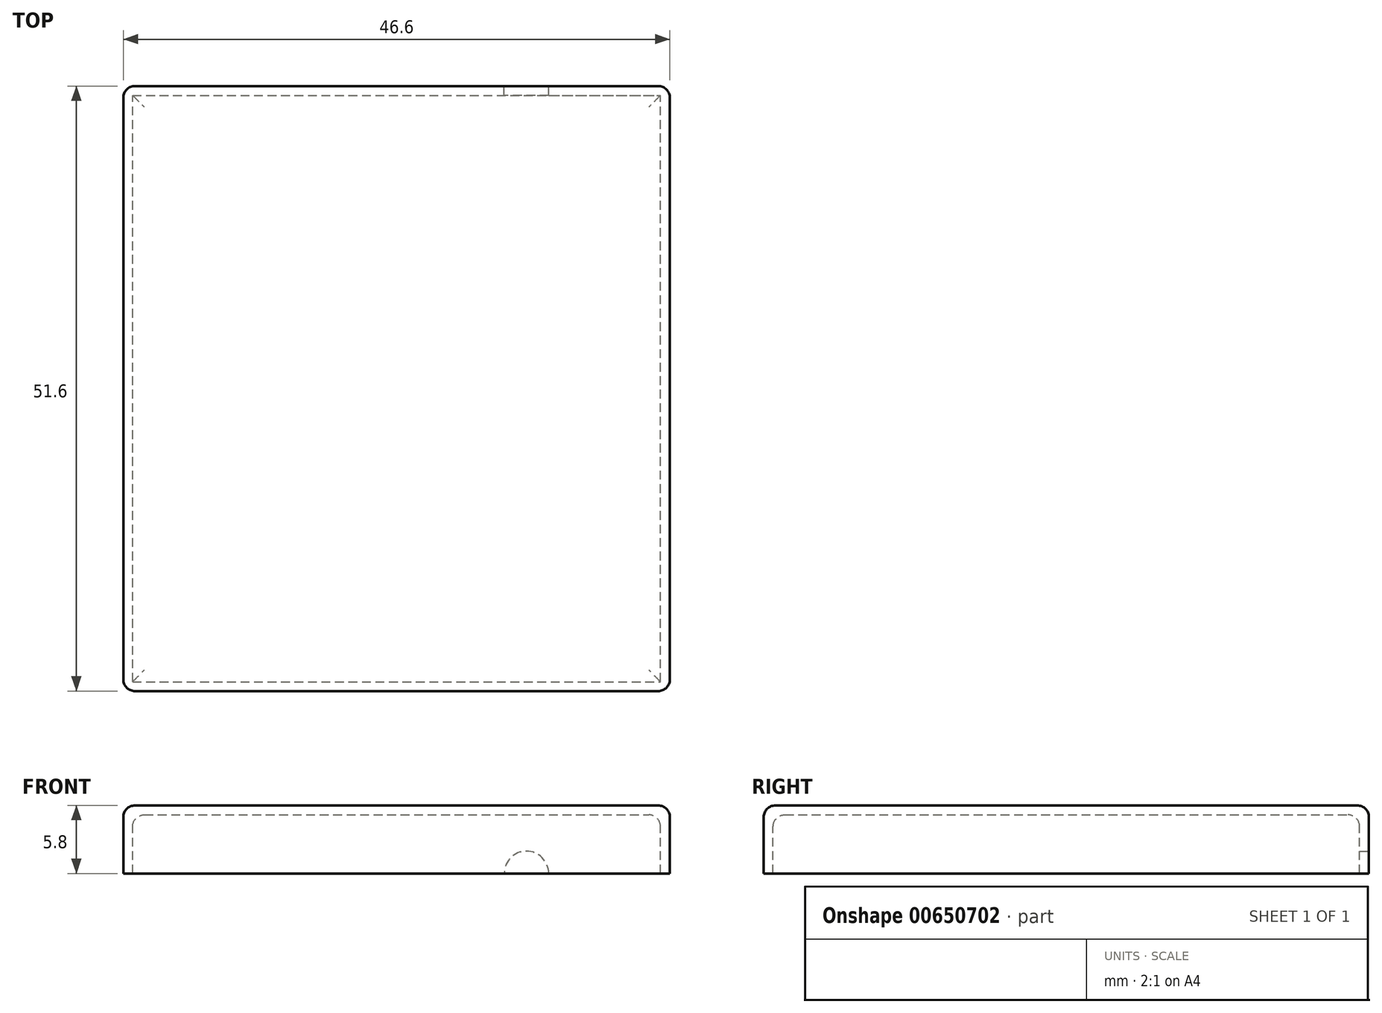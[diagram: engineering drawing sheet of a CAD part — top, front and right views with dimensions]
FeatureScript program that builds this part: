
annotation { "Feature Type Name" : "Feature", "Feature Type Description" : "" }
export const myFeature = defineFeature(function(context is Context, id is Id, definition is map)
    precondition{}
    {
        {
            var Q0;
            Q0=qCreatedBy(makeId("Top.planeOp"),FACE);
            var sketch = newSketch(context, id + "F0", { "sketchPlane" : qUnion([Q0])});
            skLineSegment(sketch, "E0.bottom", {"start": v(0, 0) * mm, "end": v(45, 0) * mm});
            skLineSegment(sketch, "E0.top", {"start": v(0, 50) * mm, "end": v(45, 50) * mm});
            skLineSegment(sketch, "E0.left", {"start": v(0, 0) * mm, "end": v(0, 50) * mm});
            skLineSegment(sketch, "E0.right", {"start": v(45, 0) * mm, "end": v(45, 50) * mm});
            skLineSegment(sketch, "E1.0", {"start": v(-0.8, -0.8) * mm, "end": v(-0.8, 50.8) * mm});
            skLineSegment(sketch, "E1.1", {"start": v(-0.8, -0.8) * mm, "end": v(45.8, -0.8) * mm});
            skLineSegment(sketch, "E1.2", {"start": v(45.8, -0.8) * mm, "end": v(45.8, 50.8) * mm});
            skLineSegment(sketch, "E1.3", {"start": v(-0.8, 50.8) * mm, "end": v(45.8, 50.8) * mm});
            skSolve(sketch);
        }
        {
            var Q0;
            Q0=makeQuery(id+"F0.imprint","IMPRINT",FACE,{"disambiguationData":[TD([[makeQuery(id+"F0.imprint","IMPRINT",EDGE,{"derivedFrom":sQuery(id+"F0.wireOp",EDGE,"E0.bottom")}),1.0]])]});
            var Q1;
            Q1=makeQuery(id+"F0.imprint","IMPRINT",FACE,{"disambiguationData":[TD([[makeQuery(id+"F0.imprint","IMPRINT",EDGE,{"derivedFrom":sQuery(id+"F0.wireOp",EDGE,"E0.bottom")}),-1.0]])]});
            extrude(context, id + "F1", {"entities" : qUnion([Q0, Q1]), "depth" : 0.8 * mm, "offsetDistance" : 25 * mm});
        }
        {
            var Q0;
            Q0=makeQuery(id+"F0.imprint","IMPRINT",FACE,{"disambiguationData":[TD([[makeQuery(id+"F0.imprint","IMPRINT",EDGE,{"derivedFrom":sQuery(id+"F0.wireOp",EDGE,"E0.bottom")}),-1.0]])]});
            extrude(context, id + "F2", {"entities" : qUnion([Q0]), "operationType" : NewBodyOperationType.ADD, "oppositeDirection" : true, "depth" : 5 * mm, "offsetDistance" : 25 * mm});
        }
        {
            var Q0;
            {var subQ0=sQuery(id+"F0.wireOp",EDGE,"E1.3");Q0=makeQuery(id+"F2.boolean.opBoolean","MERGE",FACE,{"derivedFrom":[makeQuery(id+"F1.opExtrude","SWEPT_FACE",FACE,{"disambiguationData":[OSD([subQ0])]}),makeQuery(id+"F2.opExtrude","SWEPT_FACE",FACE,{"disambiguationData":[OSD([subQ0])]})]});}
            var sketch = newSketch(context, id + "F3", { "sketchPlane" : qUnion([Q0])});
            skCircle(sketch, "E2", {"center": v(-33.57, -5) * mm, "radius": 1.9 * mm});
            skSolve(sketch);
        }
        {
            var Q0;
            {var subQ0=sQuery(id+"F3.wireOp",EDGE,"E2");var subQ1=makeQuery(id+"F2.opExtrude","CAP_EDGE",EDGE,{"disambiguationData":[OSD([sQuery(id+"F0.wireOp",EDGE,"E1.3")])],"isStart":false});var subQ2=makeQuery(id+"F3.imprint","INTERSECT",VERTEX,{"disambiguationData":[OD(0.0)],"derivedFrom":[subQ1,subQ0]});Q0=makeQuery(id+"F3.imprint","IMPRINT",FACE,{"disambiguationData":[TD([[makeQuery(id+"F3.imprint","IMPRINT",EDGE,{"disambiguationData":[TD([[subQ2,-1.0]])],"derivedFrom":subQ0}),1.0]])]});}
            var Q1;
            {var subQ0=sQuery(id+"F3.wireOp",EDGE,"E2");var subQ1=makeQuery(id+"F2.opExtrude","CAP_EDGE",EDGE,{"disambiguationData":[OSD([sQuery(id+"F0.wireOp",EDGE,"E1.3")])],"isStart":false});var subQ2=makeQuery(id+"F3.imprint","INTERSECT",VERTEX,{"disambiguationData":[OD(0.0)],"derivedFrom":[subQ1,subQ0]});Q1=makeQuery(id+"F3.imprint","IMPRINT",FACE,{"disambiguationData":[TD([[makeQuery(id+"F3.imprint","IMPRINT",EDGE,{"disambiguationData":[TD([[subQ2,1.0]])],"derivedFrom":subQ0}),1.0]])]});}
            var Q2;
            Q2=makeQuery(id+"F2.opExtrude","SWEPT_FACE",FACE,{"disambiguationData":[OSD([sQuery(id+"F0.wireOp",EDGE,"E0.top")])]});
            extrude(context, id + "F4", {"entities" : qUnion([Q0, Q1]), "operationType" : NewBodyOperationType.REMOVE, "endBound" : BoundingType.UP_TO_SURFACE, "oppositeDirection" : true, "depth" : 25 * mm, "endBoundEntityFace" : qUnion([Q2]), "offsetDistance" : 25 * mm});
        }
        {
            var Q0;
            Q0=makeQuery(id+"F1.opExtrude","CAP_FACE",FACE,{"disambiguationData":[OSD([sQuery(id+"F0.wireOp",EDGE,"E1.0"),sQuery(id+"F0.wireOp",EDGE,"E1.1"),sQuery(id+"F0.wireOp",EDGE,"E1.2"),sQuery(id+"F0.wireOp",EDGE,"E1.3")])],"isStart":false});
            var Q1;
            {var subQ0=sQuery(id+"F0.wireOp",EDGE,"E1.3");var subQ1=sQuery(id+"F0.wireOp",EDGE,"E1.0");Q1=makeQuery(id+"F2.boolean.opBoolean","MERGE",EDGE,{"derivedFrom":[makeQuery(id+"F1.opExtrude","SWEPT_EDGE",EDGE,{"disambiguationData":[OSD([subQ1,subQ0])]}),makeQuery(id+"F2.opExtrude","SWEPT_EDGE",EDGE,{"disambiguationData":[OSD([subQ1,subQ0])]})]});}
            var Q2;
            {var subQ0=sQuery(id+"F0.wireOp",EDGE,"E1.3");var subQ1=sQuery(id+"F0.wireOp",EDGE,"E1.2");Q2=makeQuery(id+"F2.boolean.opBoolean","MERGE",EDGE,{"derivedFrom":[makeQuery(id+"F1.opExtrude","SWEPT_EDGE",EDGE,{"disambiguationData":[OSD([subQ1,subQ0])]}),makeQuery(id+"F2.opExtrude","SWEPT_EDGE",EDGE,{"disambiguationData":[OSD([subQ1,subQ0])]})]});}
            var Q3;
            {var subQ0=sQuery(id+"F0.wireOp",EDGE,"E1.1");var subQ1=sQuery(id+"F0.wireOp",EDGE,"E1.0");Q3=makeQuery(id+"F2.boolean.opBoolean","MERGE",EDGE,{"derivedFrom":[makeQuery(id+"F1.opExtrude","SWEPT_EDGE",EDGE,{"disambiguationData":[OSD([subQ1,subQ0])]}),makeQuery(id+"F2.opExtrude","SWEPT_EDGE",EDGE,{"disambiguationData":[OSD([subQ1,subQ0])]})]});}
            var Q4;
            {var subQ0=sQuery(id+"F0.wireOp",EDGE,"E1.2");var subQ1=sQuery(id+"F0.wireOp",EDGE,"E1.1");Q4=makeQuery(id+"F2.boolean.opBoolean","MERGE",EDGE,{"derivedFrom":[makeQuery(id+"F1.opExtrude","SWEPT_EDGE",EDGE,{"disambiguationData":[OSD([subQ1,subQ0])]}),makeQuery(id+"F2.opExtrude","SWEPT_EDGE",EDGE,{"disambiguationData":[OSD([subQ1,subQ0])]})]});}
            var Q5;
            Q5=makeQuery(id+"F1.opExtrude","CAP_FACE",FACE,{"disambiguationData":[OSD([sQuery(id+"F0.wireOp",EDGE,"E1.0"),sQuery(id+"F0.wireOp",EDGE,"E1.1"),sQuery(id+"F0.wireOp",EDGE,"E1.2"),sQuery(id+"F0.wireOp",EDGE,"E1.3")])],"isStart":true});
            fillet(context, id + "F5", {"entities" : qUnion([Q0, Q1, Q2, Q3, Q4, Q5]), "radius" : 1 * mm, "tangentPropagation" : true, "allowEdgeOverflow" : false});
        }
    });
